# Revit family: VL2_DN15-DN100_AMV(E) 438 SU_RFA_2
name_source: partatom
category: Pipe Accessories
units: mm (PartAtom-declared; Revit-internal decimal feet)

## family parameters
Always vertical = Yes
Cut with Voids When Loaded = No
OmniClass Number = 23.65.55.14.17
OmniClass Title = Adjusting/Controlling Valves for Liquid Services
Part Type = Valve - Breaks Into
Round Connector Dimension = Use Diameter
Shared = No
Work Plane-Based = No

## types (13) — shared parameters
082H0121 = AMV(E) 438 SU_RFA : AME 438 SU_24V_082H0121
082H0123 = AMV(E) 438 SU_RFA : AMV 438 SU_230V_082H0123
Actuator Type = AMV(E) 438 SU_RFA : AMV 438 SU_24V_082H0122
Adapter Type = Adapter_AMV(E)_RFA : Adapter_AMV(E) 15(25)(35)_DN15-50_065Z0311
Connection = Flange
Description = Motorized Control Valve
IfcExportAs = IfcValveType
IfcExportType = VL2
LOD 200 = No
LOD 350 = Yes
Manufacturer = Danfoss
Max Medium Temperature = 120 °C
Min Medium Temperature = 2 °C
Nominal Pressure = PN 6
Power = 12 VA
URL = https://store.danfoss.com
V100_LOD 200 = No
V_SMALL LOD 200 = No
Valve Body Material = Danfoss Grey Iron
Voltage = 24 V

## per-type parameters (varying)
- VL2_DN25_Kvs10_065Z0377: A1=12 mm  [stored 0.0393701 ft]; A1_Flow Pipe=169.00°; A2=15.00°; A2_2=0.00°; A2_Flow Pipe=165.00°; A3=15.00°; Arc_100=1 mm  [stored 0.00328084 ft]; Assembly point=1 mm  [stored 0.00328084 ft]; D=25 mm  [stored 0.082021 ft]; D1=50 mm; DN15 to DN50=Yes; D_Connection End=62 mm; D_Flange=100 mm; Depth Flange_ve=-14 mm  [stored -0.0459318 ft]; Depth_Flange=14 mm  [stored 0.0459318 ft]; EXT2=15 mm  [stored 0.0492126 ft]; EXT200=44 mm; Extrusion Bottom=30 mm; Extrusion Top=28 mm  [stored 0.0918635 ft]; Extrusion Top 2=5 mm  [stored 0.0164042 ft]; H1=91 mm; H2=50 mm; HB=30 mm; HB1=35 mm; HB2=1 mm  [stored 0.00328084 ft]; HE=0 mm  [stored 0 ft]; HE1=61 mm; HE2=37 mm; HE_100=3 mm  [stored 0.00984252 ft]; HS_100=0 mm  [stored 0 ft]; H_Revolve Bottom=33 mm; H_Revolve Top=25 mm  [stored 0.082021 ft]; Kvs=10.0 m³/h; L=160 mm; L1=3 mm  [stored 0.00984252 ft]; L1_ve=-3 mm  [stored -0.00984252 ft]; L2=80 mm; LE1_100=20 mm  [stored 0.0656168 ft]; LE_100=10 mm  [stored 0.0328084 ft]; L_100=10 mm  [stored 0.0328084 ft]; L_EXT=90 mm; L_S=48 mm; L_Top=3 mm  [stored 0.00984252 ft]; Model=065Z0377; Model Type=VL2_DN25_Kvs10; Offset Flow Pipe_1=9 mm  [stored 0.0295276 ft]; Offset Flow Pipe_2=6 mm  [stored 0.019685 ft]; R1_Revolve=13 mm  [stored 0.0426509 ft]; R2_Revolve=10 mm  [stored 0.0328084 ft]; RB=1 mm  [stored 0.00328084 ft]; RB2=1 mm  [stored 0.00328084 ft]; RT1=25 mm  [stored 0.082021 ft]; RT1_1=21 mm  [stored 0.0688976 ft]; RT2=21 mm  [stored 0.0688976 ft]; RT3=13 mm  [stored 0.0426509 ft]; R_Arc=36 mm; R_Flow Pipe=19 mm  [stored 0.062336 ft]; R_Top=13 mm  [stored 0.0426509 ft]; Stroke=10 mm; V100=No; V2=No; V_SMALL=Yes; W=138 mm; W1=18 mm  [stored 0.0590551 ft]; W2=23 mm  [stored 0.0754593 ft]; Weight=2.59 kg
- VL2_DN32_Kvs16_065Z0378: A1=13 mm  [stored 0.0426509 ft]; A1_Flow Pipe=170.00°; A2=13.00°; A2_2=0.00°; A2_Flow Pipe=168.00°; A3=15.00°; Arc_100=1 mm  [stored 0.00328084 ft]; Assembly point=1 mm  [stored 0.00328084 ft]; D=32 mm; D1=64 mm; DN15 to DN50=Yes; D_Connection End=72 mm; D_Flange=120 mm; Depth Flange_ve=-16 mm  [stored -0.0524934 ft]; Depth_Flange=16 mm  [stored 0.0524934 ft]; EXT2=25 mm  [stored 0.082021 ft]; EXT200=49 mm; Extrusion Bottom=30 mm; Extrusion Top=34 mm; Extrusion Top 2=10 mm  [stored 0.0328084 ft]; H1=96 mm; H2=60 mm; HB=30 mm; HB1=35 mm; HB2=1 mm  [stored 0.00328084 ft]; HE=1 mm  [stored 0.00328084 ft]; HE1=65 mm; HE2=42 mm; HE_100=3 mm  [stored 0.00984252 ft]; HS_100=0 mm  [stored 0 ft]; H_Revolve Bottom=35 mm; H_Revolve Top=33 mm; Kvs=16.0 m³/h; L=180 mm; L1=3 mm  [stored 0.00984252 ft]; L1_ve=-3 mm  [stored -0.00984252 ft]; L2=90 mm; LE1_100=20 mm  [stored 0.0656168 ft]; LE_100=10 mm  [stored 0.0328084 ft]; L_100=10 mm  [stored 0.0328084 ft]; L_EXT=100 mm; L_S=48 mm; L_Top=3 mm  [stored 0.00984252 ft]; Model=065Z0378; Model Type=VL2_DN32_Kvs16; Offset Flow Pipe_1=7 mm  [stored 0.0229659 ft]; Offset Flow Pipe_2=7 mm  [stored 0.0229659 ft]; R1_Revolve=19 mm  [stored 0.062336 ft]; R2_Revolve=18 mm  [stored 0.0590551 ft]; RB=1 mm  [stored 0.00328084 ft]; RB2=1 mm  [stored 0.00328084 ft]; RT1=29 mm  [stored 0.0951444 ft]; RT1_1=24 mm  [stored 0.0787402 ft]; RT2=24 mm  [stored 0.0787402 ft]; RT3=23 mm  [stored 0.0754593 ft]; R_Arc=41 mm; R_Flow Pipe=24 mm  [stored 0.0787402 ft]; R_Top=13 mm  [stored 0.0426509 ft]; Stroke=15 mm; V100=No; V2=No; V_SMALL=Yes; W=138 mm; W1=15 mm  [stored 0.0492126 ft]; W2=27 mm  [stored 0.0885827 ft]; Weight=3.82 kg
- VL2_DN40_Kvs25_065Z0379: A1=20 mm  [stored 0.0656168 ft]; A1_Flow Pipe=168.00°; A2=20.00°; A2_2=0.00°; A2_Flow Pipe=168.00°; A3=15.00°; Arc_100=1 mm  [stored 0.00328084 ft]; Assembly point=0 mm  [stored 0 ft]; D=40 mm; D1=80 mm; DN15 to DN50=Yes; D_Connection End=82 mm; D_Flange=130 mm; Depth Flange_ve=-16 mm  [stored -0.0524934 ft]; Depth_Flange=16 mm  [stored 0.0524934 ft]; EXT2=30 mm; EXT200=54 mm; Extrusion Bottom=37 mm; Extrusion Top=38 mm; Extrusion Top 2=10 mm  [stored 0.0328084 ft]; H1=106 mm; H2=65 mm; HB=30 mm; HB1=35 mm; HB2=1 mm  [stored 0.00328084 ft]; HE=5 mm  [stored 0.0164042 ft]; HE1=76 mm; HE2=48 mm; HE_100=3 mm  [stored 0.00984252 ft]; HS_100=0 mm  [stored 0 ft]; H_Revolve Bottom=44 mm; H_Revolve Top=42 mm; Kvs=25.0 m³/h; L=200 mm; L1=3 mm  [stored 0.00984252 ft]; L1_ve=-3 mm  [stored -0.00984252 ft]; L2=100 mm; LE1_100=20 mm  [stored 0.0656168 ft]; LE_100=10 mm  [stored 0.0328084 ft]; L_100=10 mm  [stored 0.0328084 ft]; L_EXT=120 mm; L_S=48 mm; L_Top=3 mm  [stored 0.00984252 ft]; Model=065Z0379; Model Type=VL2_DN40_Kvs25; Offset Flow Pipe_1=9 mm  [stored 0.0295276 ft]; Offset Flow Pipe_2=10 mm  [stored 0.0328084 ft]; R1_Revolve=21 mm  [stored 0.0688976 ft]; R2_Revolve=21 mm  [stored 0.0688976 ft]; RB=1 mm  [stored 0.00328084 ft]; RB2=1 mm  [stored 0.00328084 ft]; RT1=37 mm; RT1_1=29 mm  [stored 0.0951444 ft]; RT2=29 mm  [stored 0.0951444 ft]; RT3=19 mm  [stored 0.062336 ft]; R_Arc=50 mm; R_Flow Pipe=29 mm  [stored 0.0951444 ft]; R_Top=13 mm  [stored 0.0426509 ft]; Stroke=15 mm; V100=No; V2=No; V_SMALL=Yes; W=138 mm; W1=18 mm  [stored 0.0590551 ft]; W2=31 mm; Weight=5.28 kg
- VL2_DN50_Kvs40_065Z0380: A1=15 mm  [stored 0.0492126 ft]; A1_Flow Pipe=170.00°; A2=18.00°; A2_2=0.00°; A2_Flow Pipe=166.00°; A3=13.00°; Arc_100=1 mm  [stored 0.00328084 ft]; Assembly point=0 mm  [stored 0 ft]; D=50 mm; D1=100 mm; DN15 to DN50=Yes; D_Connection End=93 mm; D_Flange=140 mm; Depth Flange_ve=-16 mm  [stored -0.0524934 ft]; Depth_Flange=16 mm  [stored 0.0524934 ft]; EXT2=30 mm; EXT200=59 mm; Extrusion Bottom=41 mm; Extrusion Top=41 mm; Extrusion Top 2=10 mm  [stored 0.0328084 ft]; H1=111 mm; H2=70 mm; HB=30 mm; HB1=35 mm; HB2=1 mm  [stored 0.00328084 ft]; HE=6 mm  [stored 0.019685 ft]; HE1=81 mm; HE2=53 mm; HE_100=3 mm  [stored 0.00984252 ft]; HS_100=0 mm  [stored 0 ft]; H_Revolve Bottom=53 mm; H_Revolve Top=45 mm; Kvs=40.0 m³/h; L=230 mm; L1=4 mm  [stored 0.0131234 ft]; L1_ve=-4 mm  [stored -0.0131234 ft]; L2=115 mm; LE1_100=20 mm  [stored 0.0656168 ft]; LE_100=10 mm  [stored 0.0328084 ft]; L_100=10 mm  [stored 0.0328084 ft]; L_EXT=150 mm; L_S=65 mm; L_Top=3 mm  [stored 0.00984252 ft]; Model=065Z0380; Model Type=VL2_DN50_Kvs40; Offset Flow Pipe_1=10 mm  [stored 0.0328084 ft]; Offset Flow Pipe_2=15 mm  [stored 0.0492126 ft]; R1_Revolve=26 mm; R2_Revolve=23 mm  [stored 0.0754593 ft]; RB=1 mm  [stored 0.00328084 ft]; RB2=1 mm  [stored 0.00328084 ft]; RT1=44 mm; RT1_1=35 mm; RT2=35 mm; RT3=20 mm  [stored 0.0656168 ft]; R_Arc=59 mm; R_Flow Pipe=30 mm; R_Top=13 mm  [stored 0.0426509 ft]; Stroke=15 mm; V100=No; V2=No; V_SMALL=Yes; W=140 mm; W1=30 mm; W2=42 mm; Weight=6.74 kg
- VL2_DN65_Kvs63_065Z0381: A1=30 mm; A1_Flow Pipe=165.00°; A2=20.00°; A2_2=0.00°; A2_Flow Pipe=165.00°; A3=18.00°; Arc_100=1 mm  [stored 0.00328084 ft]; Assembly point=7 mm  [stored 0.0229659 ft]; D=65 mm; D1=130 mm; DN15 to DN50=No; D_Connection End=130 mm; D_Flange=185 mm; Depth Flange_ve=-19 mm  [stored -0.062336 ft]; Depth_Flange=19 mm  [stored 0.062336 ft]; EXT2=65 mm; EXT200=2 mm  [stored 0.00656168 ft]; Extrusion Bottom=66 mm; Extrusion Top=63 mm; Extrusion Top 2=20 mm  [stored 0.0656168 ft]; H1=148 mm; H2=93 mm; HB=60 mm; HB1=81 mm; HB2=7 mm  [stored 0.0229659 ft]; HE=20 mm  [stored 0.0656168 ft]; HE1=113 mm; HE2=68 mm; HE_100=3 mm  [stored 0.00984252 ft]; HS_100=0 mm  [stored 0 ft]; H_Revolve Bottom=66 mm; H_Revolve Top=68 mm; Kvs=63.0 m³/h; L=290 mm; L1=6 mm  [stored 0.019685 ft]; L1_ve=-6 mm; L2=145 mm; LE1_100=20 mm  [stored 0.0656168 ft]; LE_100=10 mm  [stored 0.0328084 ft]; L_100=10 mm  [stored 0.0328084 ft]; L_EXT=180 mm; L_S=97 mm; L_Top=3 mm  [stored 0.00984252 ft]; Model=065Z0381; Model Type=VL2_DN65_Kvs63; Offset Flow Pipe_1=20 mm  [stored 0.0656168 ft]; Offset Flow Pipe_2=25 mm  [stored 0.082021 ft]; R1_Revolve=27 mm  [stored 0.0885827 ft]; R2_Revolve=23 mm  [stored 0.0754593 ft]; RB=55 mm; RB2=27 mm  [stored 0.0885827 ft]; RT1=22 mm  [stored 0.0721785 ft]; RT1_1=5 mm  [stored 0.0164042 ft]; RT2=1 mm  [stored 0.00328084 ft]; RT3=22 mm  [stored 0.0721785 ft]; R_Arc=82 mm; R_Flow Pipe=41 mm; R_Top=13 mm  [stored 0.0426509 ft]; Stroke=20 mm; V100=No; V2=Yes; V_SMALL=Yes; W=185 mm; W1=40 mm; W2=58 mm; Weight=13.90 kg
- VL2_DN80_Kvs100_065Z0382: A1=22 mm  [stored 0.0721785 ft]; A1_Flow Pipe=163.00°; A2=15.00°; A2_2=0.00°; A2_Flow Pipe=169.00°; A3=15.00°; Arc_100=1 mm  [stored 0.00328084 ft]; Assembly point=7 mm  [stored 0.0229659 ft]; D=80 mm; D1=160 mm; DN15 to DN50=No; D_Connection End=138 mm; D_Flange=190 mm; Depth Flange_ve=-17 mm; Depth_Flange=17 mm; EXT2=58 mm; EXT200=1 mm  [stored 0.00328084 ft]; Extrusion Bottom=65 mm; Extrusion Top=66 mm; Extrusion Top 2=20 mm  [stored 0.0656168 ft]; H1=152 mm; H2=95 mm; HB=60 mm; HB1=86 mm; HB2=9 mm  [stored 0.0295276 ft]; HE=32 mm; HE1=118 mm; HE2=60 mm; HE_100=3 mm  [stored 0.00984252 ft]; HS_100=0 mm  [stored 0 ft]; H_Revolve Bottom=65 mm; H_Revolve Top=75 mm; Kvs=100.0 m³/h; L=310 mm; L1=5 mm  [stored 0.0164042 ft]; L1_ve=-5 mm  [stored -0.0164042 ft]; L2=155 mm; LE1_100=20 mm  [stored 0.0656168 ft]; LE_100=10 mm  [stored 0.0328084 ft]; L_100=10 mm  [stored 0.0328084 ft]; L_EXT=200 mm; L_S=95 mm; L_Top=3 mm  [stored 0.00984252 ft]; Model=065Z0382; Model Type=VL2_DN80_Kvs100; Offset Flow Pipe_1=30 mm; Offset Flow Pipe_2=21 mm  [stored 0.0688976 ft]; R1_Revolve=37 mm; R2_Revolve=32 mm; RB=63 mm; RB2=27 mm  [stored 0.0885827 ft]; RT1=22 mm  [stored 0.0721785 ft]; RT1_1=5 mm  [stored 0.0164042 ft]; RT2=1 mm  [stored 0.00328084 ft]; RT3=22 mm  [stored 0.0721785 ft]; R_Arc=91 mm; R_Flow Pipe=44 mm; R_Top=13 mm  [stored 0.0426509 ft]; Stroke=20 mm; V100=No; V2=Yes; V_SMALL=Yes; W=190 mm; W1=43 mm; W2=64 mm; Weight=17.22 kg
- VL2_DN100_Kvs145_065Z3426: A1=43 mm; A1_Flow Pipe=165.00°; A2=45.00°; A2_2=44.00°; A2_Flow Pipe=164.00°; A3=0.00°; Arc_100=30 mm; Assembly point=0 mm  [stored 0 ft]; D=100 mm; D1=200 mm; DN15 to DN50=No; D_Connection End=160 mm; D_Flange=210 mm; Depth Flange_ve=-21 mm  [stored -0.0688976 ft]; Depth_Flange=21 mm  [stored 0.0688976 ft]; EXT2=0 mm  [stored 0 ft]; EXT200=1 mm  [stored 0.00328084 ft]; Extrusion Bottom=152 mm; Extrusion Top=67 mm; Extrusion Top 2=20 mm  [stored 0.0656168 ft]; H1=161 mm; H2=195 mm; HB=70 mm; HB1=151 mm; HB2=44 mm; HE=33 mm; HE1=117 mm; HE2=45 mm; HE_100=73 mm; HS_100=-73 mm; H_Revolve Bottom=50 mm; H_Revolve Top=60 mm; Kvs=145.0 m³/h; L=350 mm; L1=3 mm  [stored 0.00984252 ft]; L1_ve=-3 mm  [stored -0.00984252 ft]; L2=175 mm; LE1_100=153 mm; LE_100=108 mm; L_100=170 mm; L_EXT=19 mm  [stored 0.062336 ft]; L_S=95 mm; L_Top=6 mm  [stored 0.019685 ft]; Model=065Z3426; Model Type=VL2_DN100_Kvs145; Offset Flow Pipe_1=25 mm  [stored 0.082021 ft]; Offset Flow Pipe_2=33 mm; R1_Revolve=25 mm  [stored 0.082021 ft]; R2_Revolve=25 mm  [stored 0.082021 ft]; RB=70 mm; RB2=105 mm; RT1=35 mm; RT1_1=59 mm; RT2=60 mm; RT3=35 mm; R_Arc=2 mm  [stored 0.00656168 ft]; R_Flow Pipe=47 mm; R_Top=17 mm; Stroke=30 mm; V100=Yes; V2=Yes; V_SMALL=No; W=210 mm; W1=43 mm; W2=50 mm; Weight=39.00 kg
- VL2_DN15_Kvs0.63_065Z0371: A1=19 mm  [stored 0.062336 ft]; A1_Flow Pipe=170.00°; A2=30.00°; A2_2=0.00°; A2_Flow Pipe=168.00°; A3=16.00°; Arc_100=10 mm  [stored 0.0328084 ft]; Assembly point=1 mm  [stored 0.00328084 ft]; D=15 mm  [stored 0.0492126 ft]; D1=30 mm; DN15 to DN50=Yes; D_Connection End=50 mm; D_Flange=80 mm; Depth Flange_ve=-12 mm  [stored -0.0393701 ft]; Depth_Flange=12 mm  [stored 0.0393701 ft]; EXT2=20 mm  [stored 0.0656168 ft]; EXT200=38 mm; Extrusion Bottom=26 mm; Extrusion Top=22 mm  [stored 0.0721785 ft]; Extrusion Top 2=5 mm  [stored 0.0164042 ft]; H1=85 mm; H2=40 mm; HB=20 mm  [stored 0.0656168 ft]; HB1=25 mm  [stored 0.082021 ft]; HB2=1 mm  [stored 0.00328084 ft]; HE=0 mm  [stored 0 ft]; HE1=55 mm; HE2=31 mm; HE_100=3 mm  [stored 0.00984252 ft]; HS_100=0 mm  [stored 0 ft]; H_Revolve Bottom=27 mm  [stored 0.0885827 ft]; H_Revolve Top=23 mm  [stored 0.0754593 ft]; Kvs=0.6 m³/h; L=130 mm; L1=3 mm  [stored 0.00984252 ft]; L1_ve=-3 mm  [stored -0.00984252 ft]; L2=65 mm; LE1_100=20 mm  [stored 0.0656168 ft]; LE_100=10 mm  [stored 0.0328084 ft]; L_100=25 mm  [stored 0.082021 ft]; L_EXT=80 mm; L_S=48 mm; L_Top=3 mm  [stored 0.00984252 ft]; Model=065Z0371; Model Type=VL2_DN15_Ksv0.63; Offset Flow Pipe_1=7 mm  [stored 0.0229659 ft]; Offset Flow Pipe_2=5 mm  [stored 0.0164042 ft]; R1_Revolve=9 mm  [stored 0.0295276 ft]; R2_Revolve=6 mm  [stored 0.019685 ft]; RB=1 mm  [stored 0.00328084 ft]; RB2=1 mm  [stored 0.00328084 ft]; RT1=21 mm  [stored 0.0688976 ft]; RT1_1=16 mm  [stored 0.0524934 ft]; RT2=16 mm  [stored 0.0524934 ft]; RT3=13 mm  [stored 0.0426509 ft]; R_Arc=30 mm; R_Flow Pipe=15 mm  [stored 0.0492126 ft]; R_Top=13 mm  [stored 0.0426509 ft]; Stroke=10 mm; V100=No; V2=No; V_SMALL=Yes; W=138 mm; W1=17 mm; W2=16 mm  [stored 0.0524934 ft]; Weight=1.48 kg
- VL2_DN20_Kvs6.3_065Z0376: A1=16 mm  [stored 0.0524934 ft]; A1_Flow Pipe=172.00°; A2=22.00°; A2_2=0.00°; A2_Flow Pipe=165.00°; A3=15.00°; Arc_100=1 mm  [stored 0.00328084 ft]; Assembly point=1 mm  [stored 0.00328084 ft]; D=20 mm  [stored 0.0656168 ft]; D1=40 mm; DN15 to DN50=Yes; D_Connection End=56 mm; D_Flange=90 mm; Depth Flange_ve=-14 mm  [stored -0.0459318 ft]; Depth_Flange=14 mm  [stored 0.0459318 ft]; EXT2=18 mm  [stored 0.0590551 ft]; EXT200=41 mm; Extrusion Bottom=28 mm  [stored 0.0918635 ft]; Extrusion Top=27 mm  [stored 0.0885827 ft]; Extrusion Top 2=8 mm  [stored 0.0262467 ft]; H1=87 mm; H2=45 mm; HB=30 mm; HB1=25 mm  [stored 0.082021 ft]; HB2=1 mm  [stored 0.00328084 ft]; HE=0 mm  [stored 0 ft]; HE1=57 mm; HE2=34 mm; HE_100=3 mm  [stored 0.00984252 ft]; HS_100=0 mm  [stored 0 ft]; H_Revolve Bottom=31 mm; H_Revolve Top=25 mm  [stored 0.082021 ft]; Kvs=6.3 m³/h; L=150 mm; L1=3 mm  [stored 0.00984252 ft]; L1_ve=-3 mm  [stored -0.00984252 ft]; L2=75 mm; LE1_100=20 mm  [stored 0.0656168 ft]; LE_100=10 mm  [stored 0.0328084 ft]; L_100=10 mm  [stored 0.0328084 ft]; L_EXT=85 mm; L_S=48 mm; L_Top=3 mm  [stored 0.00984252 ft]; Model=065Z0376; Model Type=VL2_DN20_Kvs6.3; Offset Flow Pipe_1=6 mm  [stored 0.019685 ft]; Offset Flow Pipe_2=6 mm  [stored 0.019685 ft]; R1_Revolve=10 mm  [stored 0.0328084 ft]; R2_Revolve=8 mm  [stored 0.0262467 ft]; RB=1 mm  [stored 0.00328084 ft]; RB2=1 mm  [stored 0.00328084 ft]; RT1=23 mm  [stored 0.0754593 ft]; RT1_1=20 mm  [stored 0.0656168 ft]; RT2=20 mm  [stored 0.0656168 ft]; RT3=13 mm  [stored 0.0426509 ft]; R_Arc=35 mm; R_Flow Pipe=17 mm; R_Top=13 mm  [stored 0.0426509 ft]; Stroke=10 mm; V100=No; V2=No; V_SMALL=Yes; W=138 mm; W1=16 mm  [stored 0.0524934 ft]; W2=19 mm  [stored 0.062336 ft]; Weight=2.07 kg
- VL2_DN15_Kvs1.0_065Z0372: A1=19 mm  [stored 0.062336 ft]; A1_Flow Pipe=170.00°; A2=30.00°; A2_2=0.00°; A2_Flow Pipe=168.00°; A3=16.00°; Arc_100=10 mm  [stored 0.0328084 ft]; Assembly point=1 mm  [stored 0.00328084 ft]; D=15 mm  [stored 0.0492126 ft]; D1=30 mm; DN15 to DN50=Yes; D_Connection End=50 mm; D_Flange=80 mm; Depth Flange_ve=-12 mm  [stored -0.0393701 ft]; Depth_Flange=12 mm  [stored 0.0393701 ft]; EXT2=20 mm  [stored 0.0656168 ft]; EXT200=38 mm; Extrusion Bottom=26 mm; Extrusion Top=22 mm  [stored 0.0721785 ft]; Extrusion Top 2=5 mm  [stored 0.0164042 ft]; H1=85 mm; H2=40 mm; HB=20 mm  [stored 0.0656168 ft]; HB1=25 mm  [stored 0.082021 ft]; HB2=1 mm  [stored 0.00328084 ft]; HE=0 mm  [stored 0 ft]; HE1=55 mm; HE2=31 mm; HE_100=3 mm  [stored 0.00984252 ft]; HS_100=0 mm  [stored 0 ft]; H_Revolve Bottom=27 mm  [stored 0.0885827 ft]; H_Revolve Top=23 mm  [stored 0.0754593 ft]; Kvs=1.0 m³/h; L=130 mm; L1=3 mm  [stored 0.00984252 ft]; L1_ve=-3 mm  [stored -0.00984252 ft]; L2=65 mm; LE1_100=20 mm  [stored 0.0656168 ft]; LE_100=10 mm  [stored 0.0328084 ft]; L_100=25 mm  [stored 0.082021 ft]; L_EXT=80 mm; L_S=48 mm; L_Top=3 mm  [stored 0.00984252 ft]; Model=065Z0372; Model Type=VL2_DN15_Kvs1.0; Offset Flow Pipe_1=7 mm  [stored 0.0229659 ft]; Offset Flow Pipe_2=5 mm  [stored 0.0164042 ft]; R1_Revolve=9 mm  [stored 0.0295276 ft]; R2_Revolve=6 mm  [stored 0.019685 ft]; RB=1 mm  [stored 0.00328084 ft]; RB2=1 mm  [stored 0.00328084 ft]; RT1=21 mm  [stored 0.0688976 ft]; RT1_1=16 mm  [stored 0.0524934 ft]; RT2=16 mm  [stored 0.0524934 ft]; RT3=13 mm  [stored 0.0426509 ft]; R_Arc=30 mm; R_Flow Pipe=15 mm  [stored 0.0492126 ft]; R_Top=13 mm  [stored 0.0426509 ft]; Stroke=10 mm; V100=No; V2=No; V_SMALL=Yes; W=138 mm; W1=17 mm; W2=16 mm  [stored 0.0524934 ft]; Weight=1.48 kg
- VL2_DN15_Kvs1.6_065Z0373: A1=19 mm  [stored 0.062336 ft]; A1_Flow Pipe=170.00°; A2=30.00°; A2_2=0.00°; A2_Flow Pipe=168.00°; A3=16.00°; Arc_100=10 mm  [stored 0.0328084 ft]; Assembly point=1 mm  [stored 0.00328084 ft]; D=15 mm  [stored 0.0492126 ft]; D1=30 mm; DN15 to DN50=Yes; D_Connection End=50 mm; D_Flange=80 mm; Depth Flange_ve=-12 mm  [stored -0.0393701 ft]; Depth_Flange=12 mm  [stored 0.0393701 ft]; EXT2=20 mm  [stored 0.0656168 ft]; EXT200=38 mm; Extrusion Bottom=26 mm; Extrusion Top=22 mm  [stored 0.0721785 ft]; Extrusion Top 2=5 mm  [stored 0.0164042 ft]; H1=85 mm; H2=40 mm; HB=20 mm  [stored 0.0656168 ft]; HB1=25 mm  [stored 0.082021 ft]; HB2=1 mm  [stored 0.00328084 ft]; HE=0 mm  [stored 0 ft]; HE1=55 mm; HE2=31 mm; HE_100=3 mm  [stored 0.00984252 ft]; HS_100=0 mm  [stored 0 ft]; H_Revolve Bottom=27 mm  [stored 0.0885827 ft]; H_Revolve Top=23 mm  [stored 0.0754593 ft]; Kvs=1.6 m³/h; L=130 mm; L1=3 mm  [stored 0.00984252 ft]; L1_ve=-3 mm  [stored -0.00984252 ft]; L2=65 mm; LE1_100=20 mm  [stored 0.0656168 ft]; LE_100=10 mm  [stored 0.0328084 ft]; L_100=25 mm  [stored 0.082021 ft]; L_EXT=80 mm; L_S=48 mm; L_Top=3 mm  [stored 0.00984252 ft]; Model=065Z0373; Model Type=VL2_DN15_Kvs1.6; Offset Flow Pipe_1=7 mm  [stored 0.0229659 ft]; Offset Flow Pipe_2=5 mm  [stored 0.0164042 ft]; R1_Revolve=9 mm  [stored 0.0295276 ft]; R2_Revolve=6 mm  [stored 0.019685 ft]; RB=1 mm  [stored 0.00328084 ft]; RB2=1 mm  [stored 0.00328084 ft]; RT1=21 mm  [stored 0.0688976 ft]; RT1_1=16 mm  [stored 0.0524934 ft]; RT2=16 mm  [stored 0.0524934 ft]; RT3=13 mm  [stored 0.0426509 ft]; R_Arc=30 mm; R_Flow Pipe=15 mm  [stored 0.0492126 ft]; R_Top=13 mm  [stored 0.0426509 ft]; Stroke=10 mm; V100=No; V2=No; V_SMALL=Yes; W=138 mm; W1=17 mm; W2=16 mm  [stored 0.0524934 ft]; Weight=1.48 kg
- VL2_DN15_Kvs2.5_065Z0374: A1=19 mm  [stored 0.062336 ft]; A1_Flow Pipe=170.00°; A2=30.00°; A2_2=0.00°; A2_Flow Pipe=168.00°; A3=16.00°; Arc_100=10 mm  [stored 0.0328084 ft]; Assembly point=1 mm  [stored 0.00328084 ft]; D=15 mm  [stored 0.0492126 ft]; D1=30 mm; DN15 to DN50=Yes; D_Connection End=50 mm; D_Flange=80 mm; Depth Flange_ve=-12 mm  [stored -0.0393701 ft]; Depth_Flange=12 mm  [stored 0.0393701 ft]; EXT2=20 mm  [stored 0.0656168 ft]; EXT200=38 mm; Extrusion Bottom=26 mm; Extrusion Top=22 mm  [stored 0.0721785 ft]; Extrusion Top 2=5 mm  [stored 0.0164042 ft]; H1=85 mm; H2=40 mm; HB=20 mm  [stored 0.0656168 ft]; HB1=25 mm  [stored 0.082021 ft]; HB2=1 mm  [stored 0.00328084 ft]; HE=0 mm  [stored 0 ft]; HE1=54 mm; HE2=31 mm; HE_100=3 mm  [stored 0.00984252 ft]; HS_100=0 mm  [stored 0 ft]; H_Revolve Bottom=27 mm  [stored 0.0885827 ft]; H_Revolve Top=23 mm  [stored 0.0754593 ft]; Kvs=2.5 m³/h; L=130 mm; L1=3 mm  [stored 0.00984252 ft]; L1_ve=-3 mm  [stored -0.00984252 ft]; L2=65 mm; LE1_100=20 mm  [stored 0.0656168 ft]; LE_100=10 mm  [stored 0.0328084 ft]; L_100=25 mm  [stored 0.082021 ft]; L_EXT=80 mm; L_S=48 mm; L_Top=3 mm  [stored 0.00984252 ft]; Model=065Z0374; Model Type=VL2_DN15_Kvs2.5; Offset Flow Pipe_1=7 mm  [stored 0.0229659 ft]; Offset Flow Pipe_2=5 mm  [stored 0.0164042 ft]; R1_Revolve=9 mm  [stored 0.0295276 ft]; R2_Revolve=6 mm  [stored 0.019685 ft]; RB=1 mm  [stored 0.00328084 ft]; RB2=1 mm  [stored 0.00328084 ft]; RT1=21 mm  [stored 0.0688976 ft]; RT1_1=16 mm  [stored 0.0524934 ft]; RT2=16 mm  [stored 0.0524934 ft]; RT3=13 mm  [stored 0.0426509 ft]; R_Arc=30 mm; R_Flow Pipe=15 mm  [stored 0.0492126 ft]; R_Top=13 mm  [stored 0.0426509 ft]; Stroke=10 mm; V100=No; V2=No; V_SMALL=Yes; W=138 mm; W1=17 mm; W2=16 mm  [stored 0.0524934 ft]; Weight=1.48 kg
- VL2_DN15_Kvs4.0_065Z0375: A1=19 mm  [stored 0.062336 ft]; A1_Flow Pipe=170.00°; A2=30.00°; A2_2=0.00°; A2_Flow Pipe=168.00°; A3=16.00°; Arc_100=10 mm  [stored 0.0328084 ft]; Assembly point=1 mm  [stored 0.00328084 ft]; D=15 mm  [stored 0.0492126 ft]; D1=30 mm; DN15 to DN50=Yes; D_Connection End=50 mm; D_Flange=80 mm; Depth Flange_ve=-12 mm  [stored -0.0393701 ft]; Depth_Flange=12 mm  [stored 0.0393701 ft]; EXT2=20 mm  [stored 0.0656168 ft]; EXT200=38 mm; Extrusion Bottom=26 mm; Extrusion Top=22 mm  [stored 0.0721785 ft]; Extrusion Top 2=5 mm  [stored 0.0164042 ft]; H1=85 mm; H2=40 mm; HB=20 mm  [stored 0.0656168 ft]; HB1=25 mm  [stored 0.082021 ft]; HB2=1 mm  [stored 0.00328084 ft]; HE=0 mm  [stored 0 ft]; HE1=55 mm; HE2=31 mm; HE_100=3 mm  [stored 0.00984252 ft]; HS_100=0 mm  [stored 0 ft]; H_Revolve Bottom=27 mm  [stored 0.0885827 ft]; H_Revolve Top=23 mm  [stored 0.0754593 ft]; Kvs=4.0 m³/h; L=130 mm; L1=3 mm  [stored 0.00984252 ft]; L1_ve=-3 mm  [stored -0.00984252 ft]; L2=65 mm; LE1_100=20 mm  [stored 0.0656168 ft]; LE_100=10 mm  [stored 0.0328084 ft]; L_100=25 mm  [stored 0.082021 ft]; L_EXT=80 mm; L_S=48 mm; L_Top=3 mm  [stored 0.00984252 ft]; Model=065Z0375; Model Type=VL2_DN15_Kvs4.0; Offset Flow Pipe_1=7 mm  [stored 0.0229659 ft]; Offset Flow Pipe_2=5 mm  [stored 0.0164042 ft]; R1_Revolve=9 mm  [stored 0.0295276 ft]; R2_Revolve=6 mm  [stored 0.019685 ft]; RB=1 mm  [stored 0.00328084 ft]; RB2=1 mm  [stored 0.00328084 ft]; RT1=21 mm  [stored 0.0688976 ft]; RT1_1=16 mm  [stored 0.0524934 ft]; RT2=16 mm  [stored 0.0524934 ft]; RT3=13 mm  [stored 0.0426509 ft]; R_Arc=30 mm; R_Flow Pipe=15 mm  [stored 0.0492126 ft]; R_Top=13 mm  [stored 0.0426509 ft]; Stroke=10 mm; V100=No; V2=No; V_SMALL=Yes; W=138 mm; W1=17 mm; W2=16 mm  [stored 0.0524934 ft]; Weight=1.48 kg

note: [stored X ft] marks values corroborated as IEEE doubles in the binary element streams (Revit-internal decimal feet)

## geometry (parser evidence)
native form markers: Sweep x10
no freeform markers — native parametric forms only
